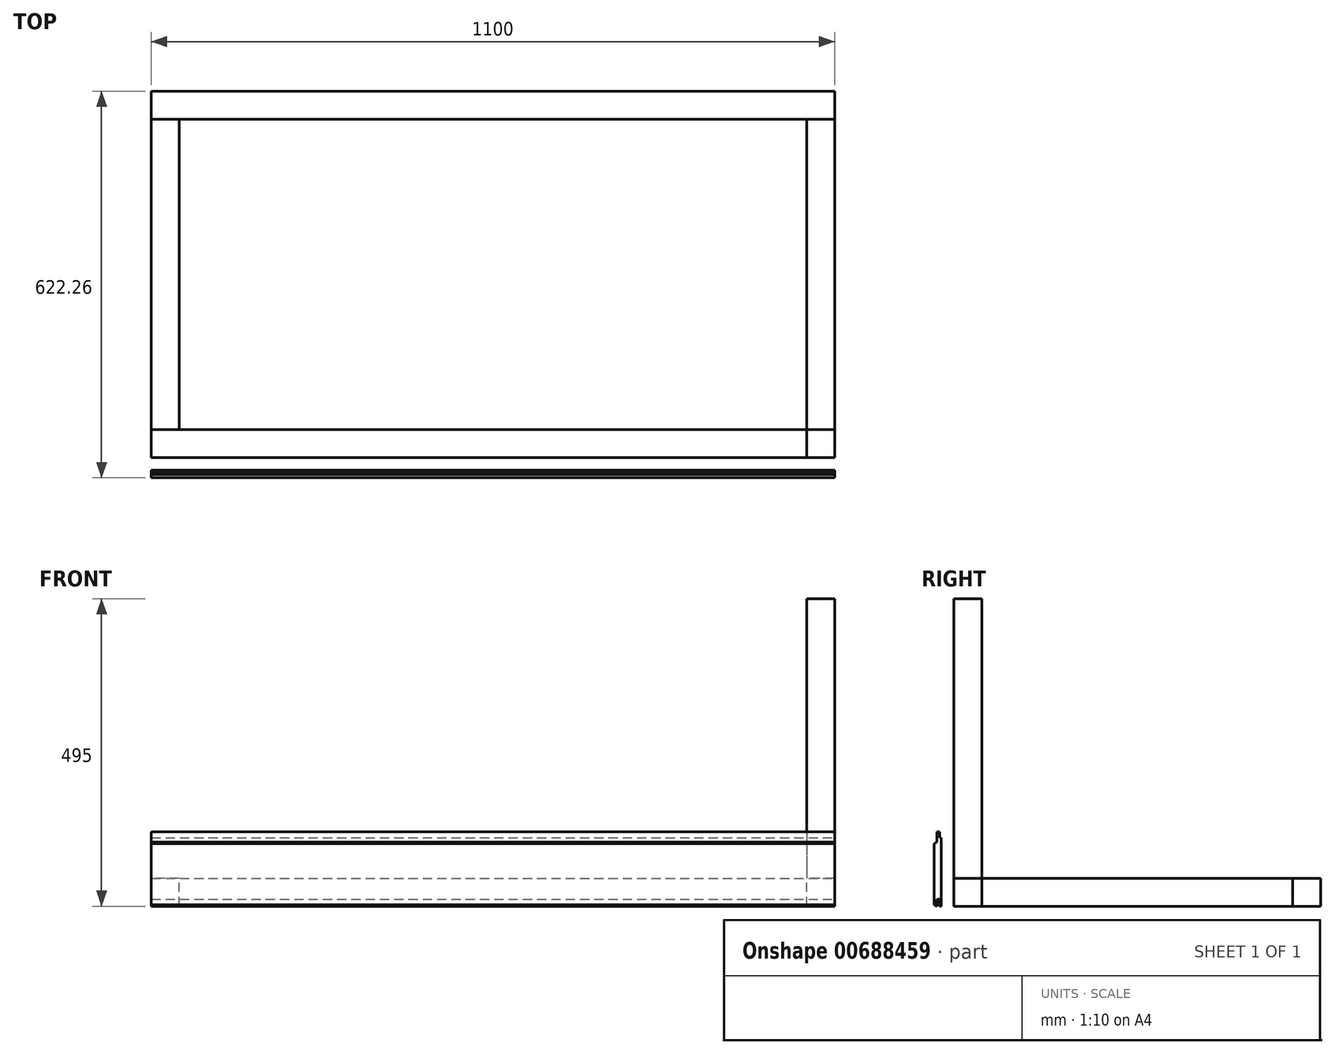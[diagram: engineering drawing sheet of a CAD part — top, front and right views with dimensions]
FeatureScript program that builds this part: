
annotation { "Feature Type Name" : "Feature", "Feature Type Description" : "" }
export const myFeature = defineFeature(function(context is Context, id is Id, definition is map)
    precondition{}
    {
        {
            var Q0;
            Q0=qCreatedBy(makeId("Front.planeOp"),FACE);
            var sketch = newSketch(context, id + "F0", { "sketchPlane" : qUnion([Q0])});
            skLineSegment(sketch, "E0.bottom", {"start": v(0, 0) * mm, "end": v(-45, 0) * mm});
            skLineSegment(sketch, "E0.top", {"start": v(0, -45) * mm, "end": v(-45, -45) * mm});
            skLineSegment(sketch, "E0.left", {"start": v(0, -45) * mm, "end": v(0, 0) * mm});
            skLineSegment(sketch, "E0.right", {"start": v(-45, -45) * mm, "end": v(-45, 0) * mm});
            skSolve(sketch);
        }
        {
            var Q0;
            Q0 = qSketchRegion(id + "F0", true);
            extrude(context, id + "F1", {"entities" : qUnion([Q0]), "oppositeDirection" : true, "depth" : 500 * mm, "offsetDistance" : 25 * mm});
        }
        {
            var Q0;
            Q0=makeQuery(id+"F1.opExtrude","SWEPT_FACE",FACE,{"disambiguationData":[OSD([sQuery(id+"F0.wireOp",EDGE,"E0.right")])]});
            var sketch = newSketch(context, id + "F2", { "sketchPlane" : qUnion([Q0])});
            skLineSegment(sketch, "E1.bottom", {"start": v(0, -45) * mm, "end": v(-45, -45) * mm});
            skLineSegment(sketch, "E1.top", {"start": v(0, 0) * mm, "end": v(-45, 0) * mm});
            skLineSegment(sketch, "E1.left", {"start": v(0, 0) * mm, "end": v(0, -45) * mm});
            skLineSegment(sketch, "E1.right", {"start": v(-45, 0) * mm, "end": v(-45, -45) * mm});
            skSolve(sketch);
        }
        {
            var Q0;
            Q0 = qSketchRegion(id + "F2", true);
            extrude(context, id + "F3", {"entities" : qUnion([Q0]), "depth" : 1100 * mm, "offsetDistance" : 25 * mm});
        }
        {
            var Q0;
            Q0=makeQuery(id+"F3.opExtrude","SWEPT_BODY",BODY,{"disambiguationData":[OSD([sQuery(id+"F2.wireOp",EDGE,"E1.bottom"),sQuery(id+"F2.wireOp",EDGE,"E1.top"),sQuery(id+"F2.wireOp",EDGE,"E1.left"),sQuery(id+"F2.wireOp",EDGE,"E1.right")])]});
            deleteBodies(context, id + "F4", {"entities" : qUnion([Q0])});
        }
        {
            var Q0;
            Q0=qCreatedBy(makeId("Right.planeOp"),FACE);
            var sketch = newSketch(context, id + "F5", { "sketchPlane" : qUnion([Q0])});
            skPoint(sketch, "E2.0", {"position": v(0, 0) * mm});
            skLineSegment(sketch, "E3.bottom", {"start": v(0, 0) * mm, "end": v(-45, 0) * mm});
            skLineSegment(sketch, "E3.top", {"start": v(0, -45) * mm, "end": v(-45, -45) * mm});
            skLineSegment(sketch, "E3.left", {"start": v(0, -45) * mm, "end": v(0, 0) * mm});
            skLineSegment(sketch, "E3.right", {"start": v(-45, -45) * mm, "end": v(-45, 0) * mm});
            skSolve(sketch);
        }
        {
            var Q0;
            Q0 = qSketchRegion(id + "F5", true);
            extrude(context, id + "F6", {"entities" : qUnion([Q0]), "oppositeDirection" : true, "depth" : 1100 * mm, "offsetDistance" : 25 * mm});
        }
        {
            var Q0;
            Q0=makeQuery(id+"F6.opExtrude","SWEPT_BODY",BODY,{"disambiguationData":[OSD([sQuery(id+"F5.wireOp",EDGE,"E3.bottom"),sQuery(id+"F5.wireOp",EDGE,"E3.top"),sQuery(id+"F5.wireOp",EDGE,"E3.left"),sQuery(id+"F5.wireOp",EDGE,"E3.right")])]});
            transform(context, id + "F7", {"entities" : qUnion([Q0]), "transformType" : TransformType.TRANSLATION_3D, "dx" : 0 * mm, "dy" : 545 * mm, "dz" : 0 * mm, "makeCopy" : true});
        }
        {
            var Q0;
            Q0=makeQuery(id+"F1.opExtrude","SWEPT_BODY",BODY,{"disambiguationData":[OSD([sQuery(id+"F0.wireOp",EDGE,"E0.bottom"),sQuery(id+"F0.wireOp",EDGE,"E0.top"),sQuery(id+"F0.wireOp",EDGE,"E0.left"),sQuery(id+"F0.wireOp",EDGE,"E0.right")])]});
            transform(context, id + "F8", {"entities" : qUnion([Q0]), "transformType" : TransformType.TRANSLATION_3D, "dx" : (-1100 + 45) * mm, "dy" : 0 * mm, "dz" : 0 * mm, "makeCopy" : true});
        }
        {
            var Q0;
            Q0=qCreatedBy(makeId("Top.planeOp"),FACE);
            var sketch = newSketch(context, id + "F9", { "sketchPlane" : qUnion([Q0])});
            skLineSegment(sketch, "E4.bottom", {"start": v(0, 0) * mm, "end": v(-45, 0) * mm});
            skLineSegment(sketch, "E4.top", {"start": v(0, -45) * mm, "end": v(-45, -45) * mm});
            skLineSegment(sketch, "E4.left", {"start": v(0, 0) * mm, "end": v(0, -45) * mm});
            skLineSegment(sketch, "E4.right", {"start": v(-45, 0) * mm, "end": v(-45, -45) * mm});
            skSolve(sketch);
        }
        {
            var Q0;
            Q0 = qSketchRegion(id + "F9", true);
            extrude(context, id + "F10", {"entities" : qUnion([Q0]), "depth" : 450 * mm, "offsetDistance" : 25 * mm});
        }
        {
            var Q0;
            Q0=qCreatedBy(makeId("Right.planeOp"),FACE);
            var sketch = newSketch(context, id + "F11", { "sketchPlane" : qUnion([Q0])});
            skPoint(sketch, "E5.0", {"position": v(-45, -45) * mm});
            skLineSegment(sketch, "E6", {"start": v(-65.26, -45) * mm, "end": v(-65.26, 65) * mm});
            skLineSegment(sketch, "E7", {"start": v(-65.26, 65) * mm, "end": v(-68.16, 65) * mm});
            skLineSegment(sketch, "E8", {"start": v(-68.16, 65) * mm, "end": v(-68.16, 75) * mm});
            skLineSegment(sketch, "E9", {"start": v(-68.16, 75) * mm, "end": v(-72.36, 75) * mm});
            skLineSegment(sketch, "E10", {"start": v(-72.36, 75) * mm, "end": v(-72.36, 58) * mm});
            skLineSegment(sketch, "E11", {"start": v(-72.36, 58) * mm, "end": v(-77.26, 55.72) * mm});
            skLineSegment(sketch, "E12", {"start": v(-77.26, 55.72) * mm, "end": v(-77.26, -42.92) * mm});
            skLineSegment(sketch, "E13", {"start": v(-77.26, -42.92) * mm, "end": v(-72.8, -45) * mm});
            skLineSegment(sketch, "E14", {"start": v(-72.8, -45) * mm, "end": v(-72.8, -34) * mm});
            skLineSegment(sketch, "E15", {"start": v(-72.8, -34) * mm, "end": v(-68.1, -34) * mm});
            skLineSegment(sketch, "E16", {"start": v(-68.1, -34) * mm, "end": v(-68.1, -45) * mm});
            skLineSegment(sketch, "E17", {"start": v(-68.1, -45) * mm, "end": v(-65.26, -45) * mm});
            skSolve(sketch);
        }
        {
            var Q0;
            Q0=makeQuery(id+"F11.imprint","IMPRINT",FACE,{"disambiguationData":[TD([[makeQuery(id+"F11.imprint","IMPRINT",EDGE,{"derivedFrom":sQuery(id+"F11.wireOp",EDGE,"E6")}),1.0]])]});
            extrude(context, id + "F12", {"entities" : qUnion([Q0]), "oppositeDirection" : true, "depth" : 1100 * mm, "offsetDistance" : 25 * mm});
        }
    });
